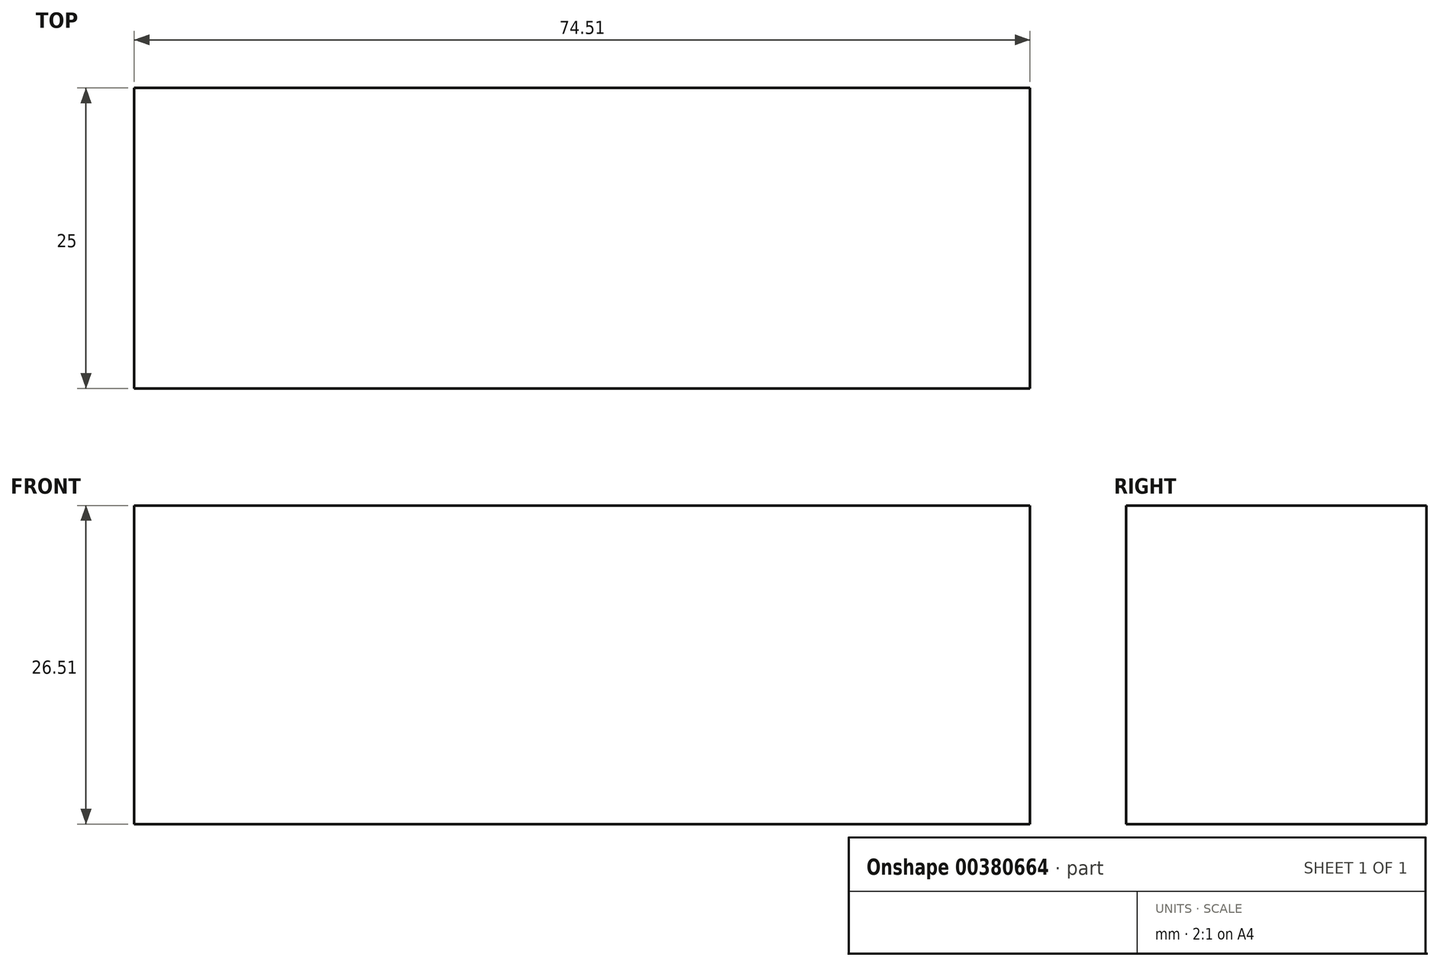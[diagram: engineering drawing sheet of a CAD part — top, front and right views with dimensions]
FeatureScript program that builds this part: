
annotation { "Feature Type Name" : "Feature", "Feature Type Description" : "" }
export const myFeature = defineFeature(function(context is Context, id is Id, definition is map)
    precondition{}
    {
        {
            var Q0;
            Q0=qCreatedBy(makeId("Front.planeOp"),FACE);
            var sketch = newSketch(context, id + "F0", { "sketchPlane" : qUnion([Q0])});
            skLineSegment(sketch, "E0.bottom", {"start": v(0, 0) * mm, "end": v(74.5, 0) * mm});
            skLineSegment(sketch, "E0.top", {"start": v(0, 26.5) * mm, "end": v(74.5, 26.5) * mm});
            skLineSegment(sketch, "E0.left", {"start": v(0, 0) * mm, "end": v(0, 26.5) * mm});
            skLineSegment(sketch, "E0.right", {"start": v(74.5, 0) * mm, "end": v(74.5, 26.5) * mm});
            skSolve(sketch);
        }
        {
            var Q0;
            Q0 = qSketchRegion(id + "F0", true);
            extrude(context, id + "F1", {"entities" : qUnion([Q0]), "depth" : 25 * mm, "offsetDistance" : 25 * mm});
        }
    });
